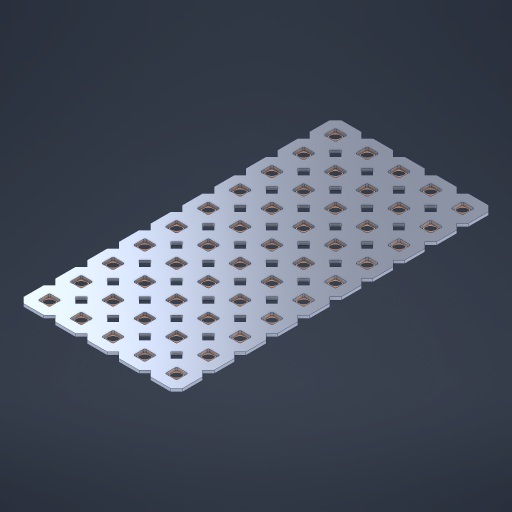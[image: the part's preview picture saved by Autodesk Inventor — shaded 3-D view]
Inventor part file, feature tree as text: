
AUTODESK INVENTOR PART (.ipt)
format: ipt  version: 2023 (Build 270158000, 158)  size: 845,312 bytes
history: native  units: in
note: dims shown in document units (in); Inventor stores cm internally (conversion verified against a paired STEP export)
features: other x51, extrude x49, sketch x2, pattern_linear x1
ambient origin geometry x8: Origin, YZ Plane, XZ Plane, XY Plane, X Axis, Y Axis, Z Axis, Center Point
bodies: Solid1 (feature_tree), Body (feature_tree)
feature tree (103):
  pattern_linear  "Rectangular Pattern1"  Spacing1=0.09in  [1 undecoded]
  sketch  "Sketch1"  dims[d1=0.5in]
  sketch  "Sketch2"  dims[d2=0.182in d3=0.09in d4=0.09in d5=0.09in d6=0.09in d7=0.09in d8=0.09in d9=0.09in d10=0.09in d11=0.02in d13=0.0in d14=0.172in d15=0.0625in d16=0.0in d19=0.5in d22=0.5in]
  other  "Srf1"
  other  "Srf126"
  other  "Srf127"
  other  "Srf128"
  other  "Srf129"
  other  "Srf130"
  other  "Srf131"
  other  "Srf250"
  other  "Srf251"
  other  "Srf252"
  other  "Srf268"
  other  "Srf269"
  other  "Srf270"
  other  "Srf271"
  other  "Srf272"
  other  "Srf273"
  other  "Srf274"
  other  "Srf275"
  other  "Srf276"
  other  "Srf277"
  other  "Srf293"
  other  "Srf294"
  other  "Srf295"
  other  "Srf296"
  other  "Srf297"
  other  "Srf298"
  other  "Srf299"
  other  "Srf300"
  other  "Srf301"
  other  "Srf302"
  other  "Srf318"
  other  "Srf319"
  other  "Srf320"
  other  "Srf321"
  other  "Srf322"
  other  "Srf323"
  other  "Srf324"
  other  "Srf325"
  other  "Srf326"
  other  "Srf327"
  other  "Srf343"
  other  "Srf344"
  other  "Srf345"
  other  "Srf346"
  other  "Srf347"
  other  "Srf348"
  other  "Srf349"
  other  "Srf350"
  other  "Srf351"
  other  "Srf352"
  other  "Circle"
  extrude  "ExtrusionSrf126"  Depth=0.09in
  extrude  "ExtrusionSrf127"  Depth=0.09in
  extrude  "ExtrusionSrf128"  Depth=0.09in
  extrude  "ExtrusionSrf129"  Depth=0.09in
  extrude  "ExtrusionSrf130"  Depth=0.09in
  extrude  "ExtrusionSrf131"  Depth=0.09in
  extrude  "ExtrusionSrf250"  Depth=0.09in
  extrude  "ExtrusionSrf251"  Depth=0.02in
  extrude  "ExtrusionSrf252"  TaperAngle=0.0deg  [1 undecoded]
  extrude  "ExtrusionSrf268"  Depth=0.5in
  extrude  "ExtrusionSrf269"  Depth=0.5in TaperAngle=0.0deg
  extrude  "ExtrusionSrf270"  Depth=0.5in
  extrude  "ExtrusionSrf271"  Depth=0.5in
  extrude  "ExtrusionSrf272"  [1 undecoded]
  extrude  "ExtrusionSrf273"  [1 undecoded]
  extrude  "ExtrusionSrf274"  [1 undecoded]
  extrude  "ExtrusionSrf275"  [1 undecoded]
  extrude  "ExtrusionSrf276"  [1 undecoded]
  extrude  "ExtrusionSrf277"  [1 undecoded]
  extrude  "ExtrusionSrf293"  [1 undecoded]
  extrude  "ExtrusionSrf294"  [1 undecoded]
  extrude  "ExtrusionSrf295"  [1 undecoded]
  extrude  "ExtrusionSrf296"  [1 undecoded]
  extrude  "ExtrusionSrf297"  [1 undecoded]
  extrude  "ExtrusionSrf298"  [1 undecoded]
  extrude  "ExtrusionSrf299"  [1 undecoded]
  extrude  "ExtrusionSrf300"  [1 undecoded]
  extrude  "ExtrusionSrf301"  [1 undecoded]
  extrude  "ExtrusionSrf302"  [1 undecoded]
  extrude  "ExtrusionSrf318"  [1 undecoded]
  extrude  "ExtrusionSrf319"  [1 undecoded]
  extrude  "ExtrusionSrf320"  [1 undecoded]
  extrude  "ExtrusionSrf321"  [1 undecoded]
  extrude  "ExtrusionSrf322"  [1 undecoded]
  extrude  "ExtrusionSrf323"  [1 undecoded]
  extrude  "ExtrusionSrf324"  [1 undecoded]
  extrude  "ExtrusionSrf325"  [1 undecoded]
  extrude  "ExtrusionSrf326"  [1 undecoded]
  extrude  "ExtrusionSrf327"  [1 undecoded]
  extrude  "ExtrusionSrf343"  [1 undecoded]
  extrude  "ExtrusionSrf344"  [1 undecoded]
  extrude  "ExtrusionSrf345"  [1 undecoded]
  extrude  "ExtrusionSrf346"  [1 undecoded]
  extrude  "ExtrusionSrf347"  [1 undecoded]
  extrude  "ExtrusionSrf348"  [1 undecoded]
  extrude  "ExtrusionSrf349"  [1 undecoded]
  extrude  "ExtrusionSrf350"  [1 undecoded]
  extrude  "ExtrusionSrf351"  [1 undecoded]
  extrude  "ExtrusionSrf352"  [1 undecoded]
note: 38 required parameter values undecoded (feature->parameter linkage not recoverable at this tier; creation-order binding heuristic only, values carry confidence <= 0.55)
